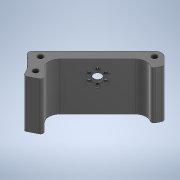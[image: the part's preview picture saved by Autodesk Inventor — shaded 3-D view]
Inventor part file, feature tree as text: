
AUTODESK INVENTOR PART (.ipt)
format: ipt  version: 2020 (Build 240168000, 168)  size: 653,824 bytes
history: native  units: mm
features: extrude x6, sketch x5, other x1, chamfer x1, fillet x1, projected_geometry x1
ambient origin geometry x8: Origin, YZ Plane, XZ Plane, XY Plane, X Axis, Y Axis, Z Axis, Center Point
bodies: Body1 (feature_tree)
feature tree (15):
  other  "Твердое тело1"
  sketch  "Эскиз1"
  extrude  "Выдавливание10"  Depth=3.8mm
  sketch  "Эскиз6"
  extrude  "Выдавливание13"  Depth=6.0mm
  extrude  "Выдавливание14"  Depth=35.0mm TaperAngle=0.0deg
  chamfer  "Фаска3"  Distance=59.0mm
  extrude  "Выдавливание15"  Depth=16.5mm
  fillet  "Сопряжение1"  Radius=10.0mm
  extrude  "Выдавливание16"  Depth=6.4mm
  extrude  "Выдавливание17"  Depth=2.3mm
  sketch  "Эскиз7"
  sketch  "Эскиз8"
  projected_geometry  "Спроецированная петля3"
  sketch  "Эскиз9"
